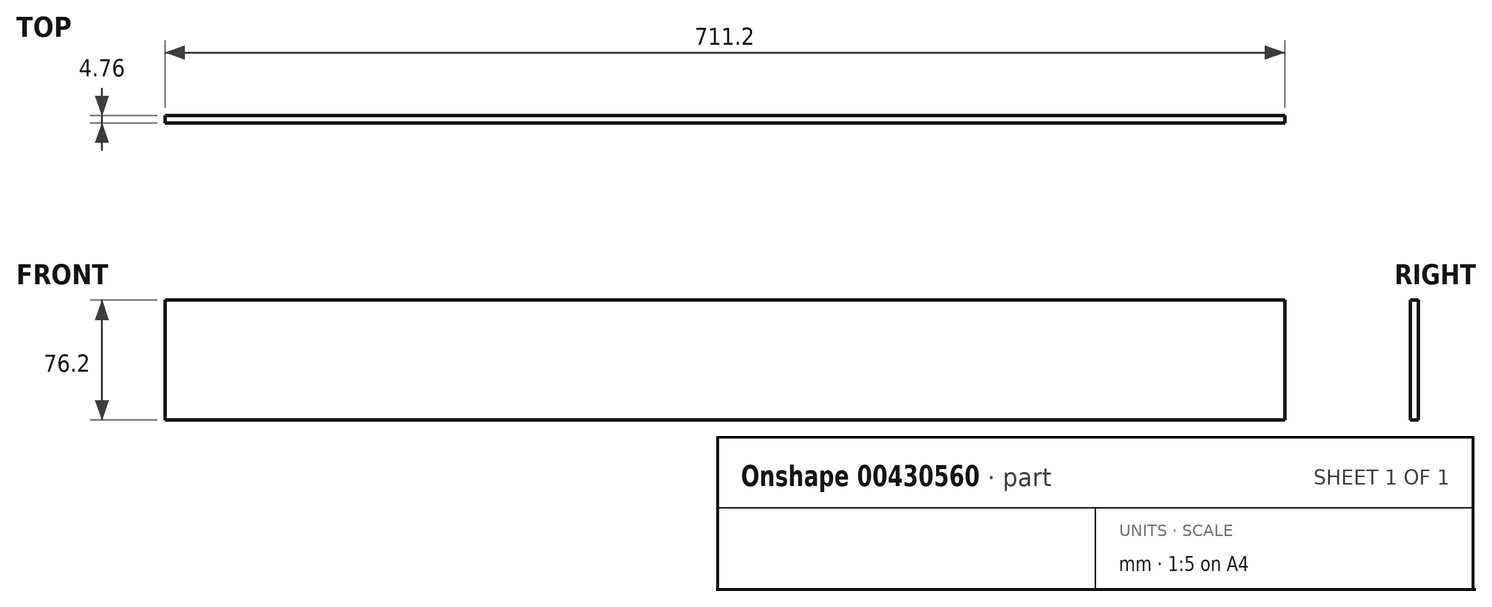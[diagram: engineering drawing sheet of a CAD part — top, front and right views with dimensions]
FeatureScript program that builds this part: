
annotation { "Feature Type Name" : "Feature", "Feature Type Description" : "" }
export const myFeature = defineFeature(function(context is Context, id is Id, definition is map)
    precondition{}
    {
        {
            var Q0;
            Q0=qCreatedBy(makeId("Front.planeOp"),FACE);
            var sketch = newSketch(context, id + "F0", { "sketchPlane" : qUnion([Q0])});
            skLineSegment(sketch, "E0.bottom", {"start": v(-121.58, 31.45) * mm, "end": v(589.62, 31.45) * mm});
            skLineSegment(sketch, "E0.top", {"start": v(-121.58, -44.75) * mm, "end": v(589.62, -44.75) * mm});
            skLineSegment(sketch, "E0.left", {"start": v(-121.58, 31.45) * mm, "end": v(-121.58, -44.75) * mm});
            skLineSegment(sketch, "E0.right", {"start": v(589.62, 31.45) * mm, "end": v(589.62, -44.75) * mm});
            skSolve(sketch);
        }
        {
            var Q0;
            Q0=makeQuery(id+"F0.imprint","IMPRINT",FACE,{"disambiguationData":[TD([[makeQuery(id+"F0.imprint","IMPRINT",EDGE,{"derivedFrom":sQuery(id+"F0.wireOp",EDGE,"E0.bottom")}),-1.0]])]});
            extrude(context, id + "F1", {"entities" : qUnion([Q0]), "depth" : 4.76 * mm});
        }
    });
